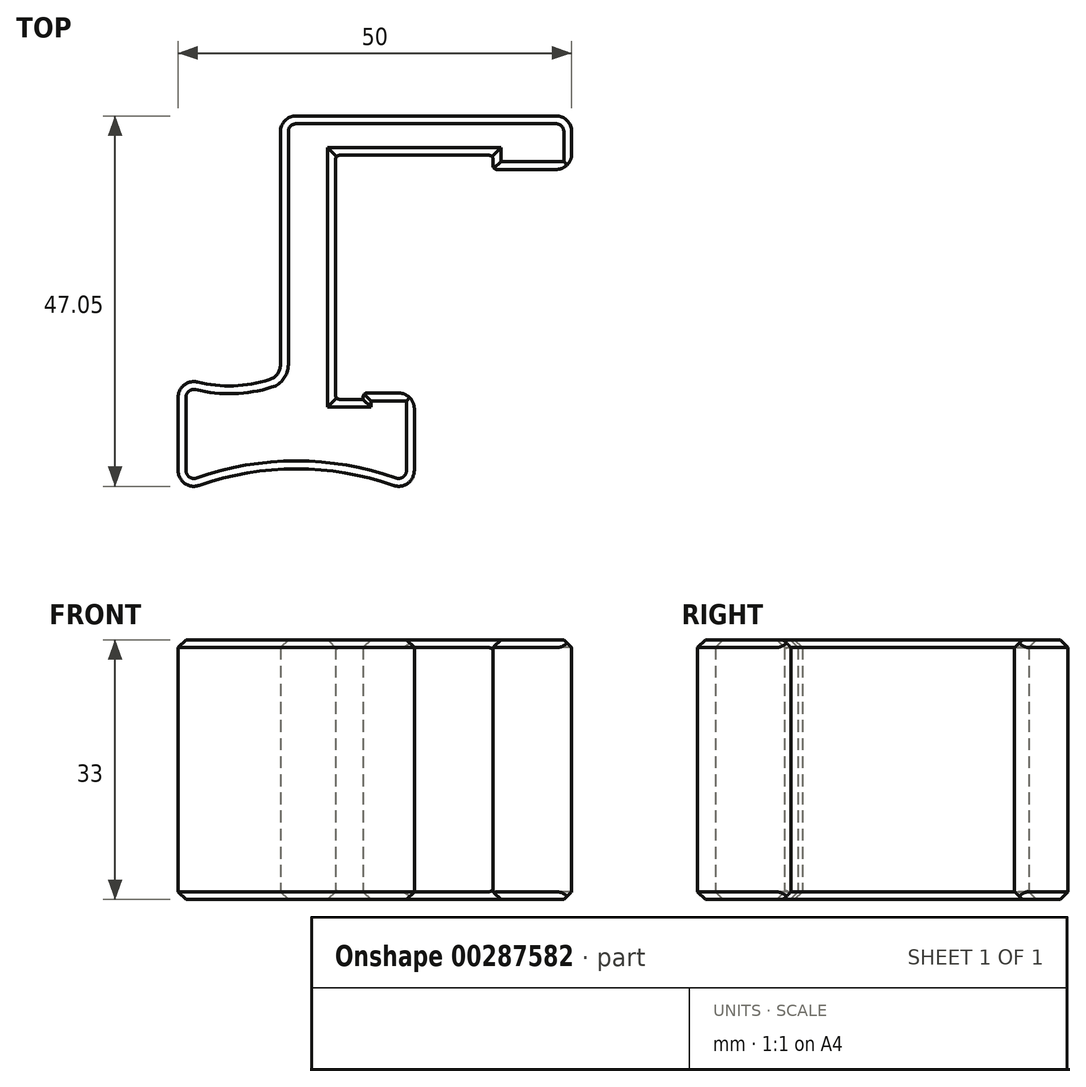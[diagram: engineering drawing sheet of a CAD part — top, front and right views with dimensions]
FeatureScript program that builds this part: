
annotation { "Feature Type Name" : "Feature", "Feature Type Description" : "" }
export const myFeature = defineFeature(function(context is Context, id is Id, definition is map)
    precondition{}
    {
        {
            var Q0;
            Q0=qCreatedBy(makeId("Top.planeOp"),FACE);
            var sketch = newSketch(context, id + "F0", { "sketchPlane" : qUnion([Q0])});
            skLineSegment(sketch, "E0.bottom", {"start": v(15, -15.5) * mm, "end": v(-15, -15.5) * mm});
            skLineSegment(sketch, "E0.left", {"start": v(15, -15.5) * mm, "end": v(15, 15.5) * mm, "construction": true});
            skLineSegment(sketch, "E0.right", {"start": v(-15, -15.5) * mm, "end": v(-15, 15.5) * mm});
            skPoint(sketch, "E0.middle", {"position": v(0, 0) * mm});
            skLineSegment(sketch, "E1", {"start": v(13, 20.5) * mm, "end": v(-20, 20.5) * mm});
            skLineSegment(sketch, "E2", {"start": v(-22, 18.5) * mm, "end": v(-22, -11.1) * mm});
            skLineSegment(sketch, "E3", {"start": v(-22, -12.5) * mm, "end": v(-35, -12.5) * mm, "construction": true});
            skLineSegment(sketch, "E4", {"start": v(-35, -15.25) * mm, "end": v(-35, -18.43) * mm});
            skLineSegment(sketch, "E5", {"start": v(-35, -18.43) * mm, "end": v(-35, -24.55) * mm});
            skLineSegment(sketch, "E6", {"start": v(-35, -27.5) * mm, "end": v(15, -27.5) * mm, "construction": true});
            skLineSegment(sketch, "E7", {"start": v(15, -27.5) * mm, "end": v(15, -15.5) * mm});
            skLineSegment(sketch, "E8", {"start": v(15, 15.5) * mm, "end": v(15, 18.5) * mm});
            skLineSegment(sketch, "E9", {"start": v(-5, -15.5) * mm, "end": v(-5, -24.55) * mm});
            skLineSegment(sketch, "E10", {"start": v(-11.5, -15.5) * mm, "end": v(-11.5, -14.7) * mm});
            skLineSegment(sketch, "E11", {"start": v(-11.5, -14.7) * mm, "end": v(-5, -14.7) * mm});
            skLineSegment(sketch, "E12", {"start": v(-5, -14.7) * mm, "end": v(-5, -15.5) * mm});
            skArc(sketch, "E13", {"start": v(-7.67, -26.44) * mm, "mid": v(-20, -24.32) * mm, "end": v(-32.33, -26.44) * mm});
            skArc(sketch, "E14", {"start": v(-32.53, -13.3) * mm, "mid": v(-27.94, -13.78) * mm, "end": v(-23.4, -13) * mm});
            skLineSegment(sketch, "E15", {"start": v(-15, 15.5) * mm, "end": v(15, 15.5) * mm, "construction": true});
            skLineSegment(sketch, "E16", {"start": v(15, 13.7) * mm, "end": v(5, 13.7) * mm});
            skLineSegment(sketch, "E17", {"start": v(5, 13.7) * mm, "end": v(5, 15.5) * mm});
            skLineSegment(sketch, "E18", {"start": v(5, 15.5) * mm, "end": v(-15, 15.5) * mm});
            skPoint(sketch, "E19.visualSharp", {"position": v(-5, -27.5) * mm});
            skArc(sketch, "E19.filletArc", {"start": v(-7.67, -26.44) * mm, "mid": v(-5.85, -26.19) * mm, "end": v(-5, -24.55) * mm});
            skPoint(sketch, "E20.visualSharp", {"position": v(-35, -27.5) * mm});
            skArc(sketch, "E20.filletArc", {"start": v(-35, -24.55) * mm, "mid": v(-34.15, -26.19) * mm, "end": v(-32.33, -26.44) * mm});
            skPoint(sketch, "E21.visualSharp", {"position": v(-35, -12.5) * mm});
            skArc(sketch, "E21.filletArc", {"start": v(-32.53, -13.3) * mm, "mid": v(-34.24, -13.68) * mm, "end": v(-35, -15.25) * mm});
            skPoint(sketch, "E22.visualSharp", {"position": v(-22, -12.5) * mm});
            skArc(sketch, "E22.filletArc", {"start": v(-23.4, -13) * mm, "mid": v(-22.39, -12.28) * mm, "end": v(-22, -11.1) * mm});
            skPoint(sketch, "E23.visualSharp", {"position": v(-22, 20.5) * mm});
            skArc(sketch, "E23.filletArc", {"start": v(-20, 20.5) * mm, "mid": v(-21.41, 19.91) * mm, "end": v(-22, 18.5) * mm});
            skPoint(sketch, "E24.visualSharp", {"position": v(15, 20.5) * mm});
            skArc(sketch, "E24.filletArc", {"start": v(15, 18.5) * mm, "mid": v(14.41, 19.91) * mm, "end": v(13, 20.5) * mm});
            skLineSegment(sketch, "E25", {"start": v(15, 13.7) * mm, "end": v(15, 15.5) * mm});
            skSolve(sketch);
        }
        {
            var Q0;
            Q0 = qSketchRegion(id + "F0", true);
            extrude(context, id + "F1", {"entities" : qUnion([Q0]), "depth" : 33 * mm, "offsetDistance" : 25 * mm});
        }
        {
            var Q0;
            Q0=makeQuery(id+"F1.opExtrude","CAP_FACE",FACE,{"disambiguationData":[OSD([sQuery(id+"F0.wireOp",EDGE,"E0.bottom"),sQuery(id+"F0.wireOp",EDGE,"E0.right"),sQuery(id+"F0.wireOp",EDGE,"E1"),sQuery(id+"F0.wireOp",EDGE,"E2"),sQuery(id+"F0.wireOp",EDGE,"E4"),sQuery(id+"F0.wireOp",EDGE,"E5"),sQuery(id+"F0.wireOp",EDGE,"E8"),sQuery(id+"F0.wireOp",EDGE,"E9"),sQuery(id+"F0.wireOp",EDGE,"E10"),sQuery(id+"F0.wireOp",EDGE,"E11"),sQuery(id+"F0.wireOp",EDGE,"E12"),sQuery(id+"F0.wireOp",EDGE,"E13"),sQuery(id+"F0.wireOp",EDGE,"E14"),sQuery(id+"F0.wireOp",EDGE,"E16"),sQuery(id+"F0.wireOp",EDGE,"E17"),sQuery(id+"F0.wireOp",EDGE,"E18"),sQuery(id+"F0.wireOp",EDGE,"E19.filletArc"),sQuery(id+"F0.wireOp",EDGE,"E20.filletArc"),sQuery(id+"F0.wireOp",EDGE,"E21.filletArc"),sQuery(id+"F0.wireOp",EDGE,"E22.filletArc"),sQuery(id+"F0.wireOp",EDGE,"E23.filletArc"),sQuery(id+"F0.wireOp",EDGE,"E24.filletArc"),sQuery(id+"F0.wireOp",EDGE,"E25")])],"isStart":false});
            var Q1;
            Q1=makeQuery(id+"F1.opExtrude","CAP_FACE",FACE,{"disambiguationData":[OSD([sQuery(id+"F0.wireOp",EDGE,"E0.bottom"),sQuery(id+"F0.wireOp",EDGE,"E0.right"),sQuery(id+"F0.wireOp",EDGE,"E1"),sQuery(id+"F0.wireOp",EDGE,"E2"),sQuery(id+"F0.wireOp",EDGE,"E4"),sQuery(id+"F0.wireOp",EDGE,"E5"),sQuery(id+"F0.wireOp",EDGE,"E8"),sQuery(id+"F0.wireOp",EDGE,"E9"),sQuery(id+"F0.wireOp",EDGE,"E10"),sQuery(id+"F0.wireOp",EDGE,"E11"),sQuery(id+"F0.wireOp",EDGE,"E12"),sQuery(id+"F0.wireOp",EDGE,"E13"),sQuery(id+"F0.wireOp",EDGE,"E14"),sQuery(id+"F0.wireOp",EDGE,"E16"),sQuery(id+"F0.wireOp",EDGE,"E17"),sQuery(id+"F0.wireOp",EDGE,"E18"),sQuery(id+"F0.wireOp",EDGE,"E19.filletArc"),sQuery(id+"F0.wireOp",EDGE,"E20.filletArc"),sQuery(id+"F0.wireOp",EDGE,"E21.filletArc"),sQuery(id+"F0.wireOp",EDGE,"E22.filletArc"),sQuery(id+"F0.wireOp",EDGE,"E23.filletArc"),sQuery(id+"F0.wireOp",EDGE,"E24.filletArc"),sQuery(id+"F0.wireOp",EDGE,"E25")])],"isStart":true});
            chamfer(context, id + "F2", {"entities" : qUnion([Q0, Q1]), "width" : 1 * mm, "tangentPropagation" : true});
        }
        {
            var Q0;
            Q0=makeQuery(id+"F1.opExtrude","SWEPT_EDGE",EDGE,{"disambiguationData":[OSD([sQuery(id+"F0.wireOp",EDGE,"E11"),sQuery(id+"F0.wireOp",EDGE,"E12")])]});
            var Q1;
            Q1=makeQuery(id+"F1.opExtrude","SWEPT_EDGE",EDGE,{"disambiguationData":[OSD([sQuery(id+"F0.wireOp",EDGE,"E16"),sQuery(id+"F0.wireOp",EDGE,"E25")])]});
            fillet(context, id + "F3", {"entities" : qUnion([Q0, Q1]), "radius" : 2 * mm, "tangentPropagation" : true, "allowEdgeOverflow" : false});
        }
        {
            var Q0;
            Q0=makeQuery(id+"F1.opExtrude","SWEPT_EDGE",EDGE,{"disambiguationData":[OSD([sQuery(id+"F0.wireOp",EDGE,"E10"),sQuery(id+"F0.wireOp",EDGE,"E11")])]});
            var Q1;
            Q1=makeQuery(id+"F1.opExtrude","SWEPT_EDGE",EDGE,{"disambiguationData":[OSD([sQuery(id+"F0.wireOp",EDGE,"E0.bottom"),sQuery(id+"F0.wireOp",EDGE,"E0.right")])]});
            var Q2;
            Q2=makeQuery(id+"F1.opExtrude","SWEPT_EDGE",EDGE,{"disambiguationData":[OSD([sQuery(id+"F0.wireOp",EDGE,"E0.right"),sQuery(id+"F0.wireOp",EDGE,"E18")])]});
            var Q3;
            Q3=makeQuery(id+"F1.opExtrude","SWEPT_EDGE",EDGE,{"disambiguationData":[OSD([sQuery(id+"F0.wireOp",EDGE,"E16"),sQuery(id+"F0.wireOp",EDGE,"E17")])]});
            var Q4;
            Q4=makeQuery(id+"F1.opExtrude","SWEPT_EDGE",EDGE,{"disambiguationData":[OSD([sQuery(id+"F0.wireOp",EDGE,"E17"),sQuery(id+"F0.wireOp",EDGE,"E18")])]});
            fillet(context, id + "F4", {"entities" : qUnion([Q0, Q1, Q2, Q3, Q4]), "radius" : 0.5 * mm, "tangentPropagation" : true, "allowEdgeOverflow" : false});
        }
    });
